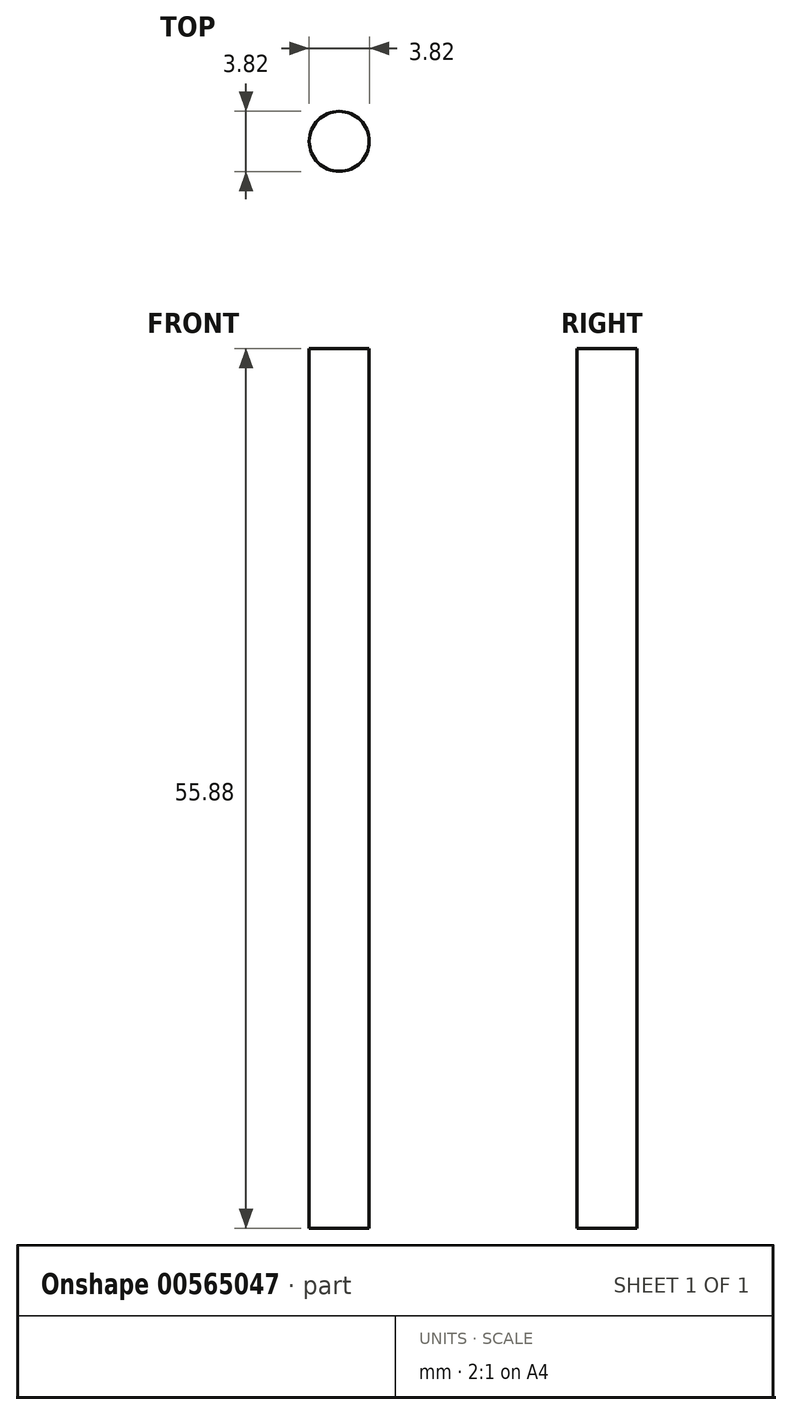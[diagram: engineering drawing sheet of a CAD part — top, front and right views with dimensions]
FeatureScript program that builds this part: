
annotation { "Feature Type Name" : "Feature", "Feature Type Description" : "" }
export const myFeature = defineFeature(function(context is Context, id is Id, definition is map)
    precondition{}
    {
        {
            var Q0;
            Q0=qCreatedBy(makeId("Top.planeOp"),FACE);
            var sketch = newSketch(context, id + "F0", { "sketchPlane" : qUnion([Q0])});
            skCircle(sketch, "E0", {"center": v(0, 0) * mm, "radius": 1.9 * mm});
            skSolve(sketch);
        }
        {
            var Q0;
            Q0 = qSketchRegion(id + "F0", true);
            extrude(context, id + "F1", {"entities" : qUnion([Q0]), "depth" : 55.88 * mm, "offsetDistance" : 25.4 * mm});
        }
    });
